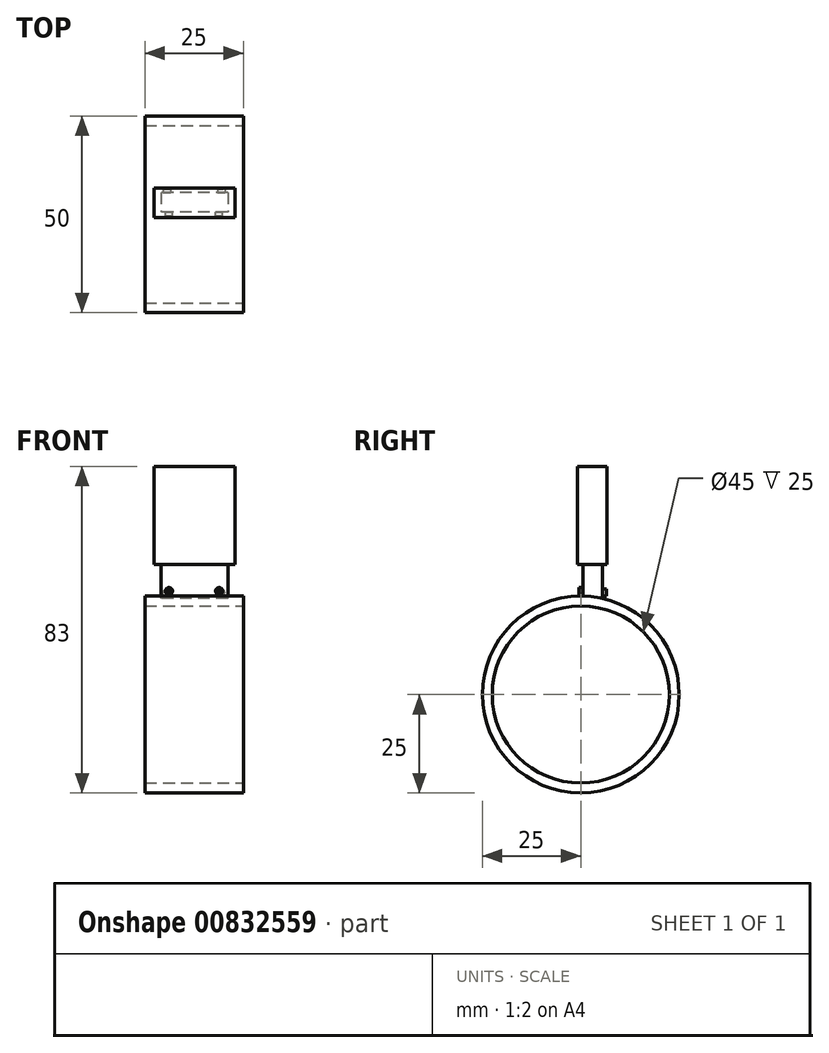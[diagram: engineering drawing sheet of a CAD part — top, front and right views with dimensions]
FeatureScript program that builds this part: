
annotation { "Feature Type Name" : "Feature", "Feature Type Description" : "" }
export const myFeature = defineFeature(function(context is Context, id is Id, definition is map)
    precondition{}
    {
        {
            var Q0;
            Q0=qCreatedBy(makeId("Right.planeOp"),FACE);
            var sketch = newSketch(context, id + "F0", { "sketchPlane" : qUnion([Q0])});
            skCircle(sketch, "E0", {"center": v(0, 0) * mm, "radius": 25 * mm});
            skSolve(sketch);
        }
        {
            var Q0;
            Q0=makeQuery(id+"F0.imprint","IMPRINT",FACE,{"disambiguationData":[TD([[makeQuery(id+"F0.imprint","IMPRINT",EDGE,{"derivedFrom":sQuery(id+"F0.wireOp",EDGE,"E0")}),1.0]])]});
            extrude(context, id + "F1", {"entities" : qUnion([Q0]), "depth" : 25 * mm, "offsetDistance" : 25 * mm});
        }
        {
            var Q0;
            Q0=makeQuery(id+"F1.opExtrude","CAP_FACE",FACE,{"disambiguationData":[OSD([sQuery(id+"F0.wireOp",EDGE,"E0")])],"isStart":false});
            var sketch = newSketch(context, id + "F2", { "sketchPlane" : qUnion([Q0])});
            skCircle(sketch, "E1", {"center": v(0, 0) * mm, "radius": 22.5 * mm});
            skSolve(sketch);
        }
        {
            var Q0;
            Q0=makeQuery(id+"F2.imprint","IMPRINT",FACE,{"disambiguationData":[TD([[makeQuery(id+"F2.imprint","IMPRINT",EDGE,{"derivedFrom":sQuery(id+"F2.wireOp",EDGE,"E1")}),1.0]])]});
            extrude(context, id + "F3", {"entities" : qUnion([Q0]), "operationType" : NewBodyOperationType.REMOVE, "oppositeDirection" : true, "depth" : 30 * mm, "offsetDistance" : 25 * mm});
        }
        {
            var Q0;
            Q0=qCreatedBy(makeId("Top.planeOp"),FACE);
            cPlane(context, id + "F4", {"entities" : qUnion([Q0]), "cplaneType" : CPlaneType.OFFSET, "offset" : 23 * mm, "width" : 150 * mm, "height" : 150 * mm});
        }
        {
            var Q0;
            Q0=qCreatedBy(id+"F4.planeOp",FACE);
            var sketch = newSketch(context, id + "F5", { "sketchPlane" : qUnion([Q0])});
            skLineSegment(sketch, "E2", {"start": v(4.05, 5.56) * mm, "end": v(4.05, 0.56) * mm});
            skLineSegment(sketch, "E3", {"start": v(4.05, 5.56) * mm, "end": v(21.05, 5.56) * mm});
            skLineSegment(sketch, "E4", {"start": v(4.05, 0.56) * mm, "end": v(21.05, 0.56) * mm});
            skLineSegment(sketch, "E5", {"start": v(21.05, 5.56) * mm, "end": v(21.05, 0.56) * mm});
            skSolve(sketch);
        }
        {
            var Q0;
            Q0 = qSketchRegion(id + "F5", true);
            extrude(context, id + "F6", {"entities" : qUnion([Q0]), "operationType" : NewBodyOperationType.ADD, "depth" : 10 * mm, "offsetDistance" : 25 * mm});
        }
        {
            var Q0;
            Q0=makeQuery(id+"F6.opExtrude","SWEPT_FACE",FACE,{"disambiguationData":[OSD([sQuery(id+"F5.wireOp",EDGE,"E3")])]});
            var sketch = newSketch(context, id + "F7", { "sketchPlane" : qUnion([Q0])});
            skCircle(sketch, "E6", {"center": v(-19.39, 25.93) * mm, "radius": 0.9 * mm});
            skCircle(sketch, "E7", {"center": v(-5.54, 25.93) * mm, "radius": 0.9 * mm});
            skSolve(sketch);
        }
        {
            var Q0;
            Q0=makeQuery(id+"F7.imprint","IMPRINT",FACE,{"disambiguationData":[TD([[makeQuery(id+"F7.imprint","IMPRINT",EDGE,{"derivedFrom":sQuery(id+"F7.wireOp",EDGE,"E6")}),1.0]])]});
            var Q1;
            Q1=makeQuery(id+"F7.imprint","IMPRINT",FACE,{"disambiguationData":[TD([[makeQuery(id+"F7.imprint","IMPRINT",EDGE,{"derivedFrom":sQuery(id+"F7.wireOp",EDGE,"E7")}),1.0]])]});
            extrude(context, id + "F8", {"entities" : qUnion([Q0, Q1]), "operationType" : NewBodyOperationType.ADD, "depth" : 1 * mm, "offsetDistance" : 25 * mm});
        }
        {
            var Q0;
            Q0=makeQuery(id+"F8.opExtrude","CAP_FACE",FACE,{"disambiguationData":[OSD([sQuery(id+"F7.wireOp",EDGE,"E6")])],"isStart":false});
            var sketch = newSketch(context, id + "F9", { "sketchPlane" : qUnion([Q0])});
            skLineSegment(sketch, "E8.bottom", {"start": v(-19.88, 25.88) * mm, "end": v(-18.78, 25.88) * mm});
            skLineSegment(sketch, "E8.top", {"start": v(-19.88, 26) * mm, "end": v(-18.78, 26) * mm});
            skLineSegment(sketch, "E8.left", {"start": v(-19.88, 25.88) * mm, "end": v(-19.88, 26) * mm});
            skLineSegment(sketch, "E8.right", {"start": v(-18.78, 25.88) * mm, "end": v(-18.78, 26) * mm});
            skLineSegment(sketch, "E9.bottom", {"start": v(-19.42, 25.36) * mm, "end": v(-19.27, 25.36) * mm});
            skLineSegment(sketch, "E9.top", {"start": v(-19.42, 26.45) * mm, "end": v(-19.27, 26.45) * mm});
            skLineSegment(sketch, "E9.left", {"start": v(-19.42, 25.36) * mm, "end": v(-19.42, 26.45) * mm});
            skLineSegment(sketch, "E9.right", {"start": v(-19.27, 25.36) * mm, "end": v(-19.27, 26.45) * mm});
            skSolve(sketch);
        }
        {
            var Q0;
            Q0 = qSketchRegion(id + "F9", true);
            extrude(context, id + "F10", {"entities" : qUnion([Q0]), "operationType" : NewBodyOperationType.REMOVE, "oppositeDirection" : true, "depth" : 0.2 * mm, "offsetDistance" : 25 * mm});
        }
        {
            var Q0;
            Q0=makeQuery(id+"F8.opExtrude","CAP_FACE",FACE,{"disambiguationData":[OSD([sQuery(id+"F7.wireOp",EDGE,"E7")])],"isStart":false});
            var sketch = newSketch(context, id + "F11", { "sketchPlane" : qUnion([Q0])});
            skLineSegment(sketch, "E10.bottom", {"start": v(-5.67, 25.28) * mm, "end": v(-5.5, 25.28) * mm});
            skLineSegment(sketch, "E10.top", {"start": v(-5.67, 26.6) * mm, "end": v(-5.5, 26.6) * mm});
            skLineSegment(sketch, "E10.left", {"start": v(-5.67, 25.28) * mm, "end": v(-5.67, 26.6) * mm});
            skLineSegment(sketch, "E10.right", {"start": v(-5.5, 25.28) * mm, "end": v(-5.5, 26.6) * mm});
            skLineSegment(sketch, "E11.bottom", {"start": v(-6.2, 25.81) * mm, "end": v(-4.92, 25.81) * mm});
            skLineSegment(sketch, "E11.top", {"start": v(-6.2, 26) * mm, "end": v(-4.92, 26) * mm});
            skLineSegment(sketch, "E11.left", {"start": v(-6.2, 25.81) * mm, "end": v(-6.2, 26) * mm});
            skLineSegment(sketch, "E11.right", {"start": v(-4.92, 25.81) * mm, "end": v(-4.92, 26) * mm});
            skSolve(sketch);
        }
        {
            var Q0;
            Q0 = qSketchRegion(id + "F11", true);
            extrude(context, id + "F12", {"entities" : qUnion([Q0]), "operationType" : NewBodyOperationType.REMOVE, "oppositeDirection" : true, "depth" : 0.2 * mm, "offsetDistance" : 25 * mm});
        }
        {
            var Q0;
            Q0=makeQuery(id+"F6.opExtrude","SWEPT_FACE",FACE,{"disambiguationData":[OSD([sQuery(id+"F5.wireOp",EDGE,"E4")])]});
            var sketch = newSketch(context, id + "F13", { "sketchPlane" : qUnion([Q0])});
            skCircle(sketch, "E12", {"center": v(6.1, 26.28) * mm, "radius": 0.9 * mm});
            skCircle(sketch, "E13", {"center": v(18.83, 26.28) * mm, "radius": 0.9 * mm});
            skSolve(sketch);
        }
        {
            var Q0;
            Q0=makeQuery(id+"F13.imprint","IMPRINT",FACE,{"disambiguationData":[TD([[makeQuery(id+"F13.imprint","IMPRINT",EDGE,{"derivedFrom":sQuery(id+"F13.wireOp",EDGE,"E12")}),1.0]])]});
            var Q1;
            Q1=makeQuery(id+"F13.imprint","IMPRINT",FACE,{"disambiguationData":[TD([[makeQuery(id+"F13.imprint","IMPRINT",EDGE,{"derivedFrom":sQuery(id+"F13.wireOp",EDGE,"E13")}),1.0]])]});
            extrude(context, id + "F14", {"entities" : qUnion([Q0, Q1]), "operationType" : NewBodyOperationType.ADD, "depth" : 1 * mm, "offsetDistance" : 25 * mm});
        }
        {
            var Q0;
            Q0=makeQuery(id+"F14.opExtrude","CAP_FACE",FACE,{"disambiguationData":[OSD([sQuery(id+"F13.wireOp",EDGE,"E12")])],"isStart":false});
            var sketch = newSketch(context, id + "F15", { "sketchPlane" : qUnion([Q0])});
            skLineSegment(sketch, "E14.bottom", {"start": v(6, 26.9) * mm, "end": v(6.13, 26.9) * mm});
            skLineSegment(sketch, "E14.top", {"start": v(6, 25.73) * mm, "end": v(6.13, 25.73) * mm});
            skLineSegment(sketch, "E14.left", {"start": v(5.96, 26.37) * mm, "end": v(5.96, 26.27) * mm});
            skLineSegment(sketch, "E14.right", {"start": v(6.2, 26.37) * mm, "end": v(6.2, 26.27) * mm});
            skLineSegment(sketch, "E15.right", {"start": v(6.73, 26.44) * mm, "end": v(6.73, 26.18) * mm});
            skLineSegment(sketch, "E16", {"start": v(5.49, 26.37) * mm, "end": v(6.73, 26.37) * mm});
            skPoint(sketch, "E16.endSnap0", {"position": v(6.73, 26.3) * mm});
            skLineSegment(sketch, "E17", {"start": v(5.49, 26.27) * mm, "end": v(6.73, 26.27) * mm});
            skLineSegment(sketch, "E18", {"start": v(6, 26.9) * mm, "end": v(6, 25.73) * mm});
            skLineSegment(sketch, "E19", {"start": v(6.13, 26.9) * mm, "end": v(6.13, 25.73) * mm});
            skLineSegment(sketch, "E20.trimOffspring", {"start": v(6, 26.44) * mm, "end": v(6.13, 26.44) * mm});
            skPoint(sketch, "E21.orphan", {"position": v(5.96, 25.73) * mm});
            skLineSegment(sketch, "E22", {"start": v(5.49, 26.37) * mm, "end": v(5.49, 26.27) * mm});
            skSolve(sketch);
        }
        {
            var Q0;
            Q0=makeQuery(id+"F14.opExtrude","CAP_FACE",FACE,{"disambiguationData":[OSD([sQuery(id+"F13.wireOp",EDGE,"E13")])],"isStart":false});
            var sketch = newSketch(context, id + "F16", { "sketchPlane" : qUnion([Q0])});
            skLineSegment(sketch, "E23.bottom", {"start": v(18.7, 26.95) * mm, "end": v(18.86, 26.95) * mm});
            skLineSegment(sketch, "E23.top", {"start": v(18.7, 25.55) * mm, "end": v(18.86, 25.55) * mm});
            skLineSegment(sketch, "E24.left", {"start": v(18.18, 26.34) * mm, "end": v(18.18, 26.21) * mm});
            skLineSegment(sketch, "E24.right", {"start": v(19.46, 26.34) * mm, "end": v(19.46, 26.21) * mm});
            skLineSegment(sketch, "E25", {"start": v(18.7, 26.95) * mm, "end": v(18.7, 25.55) * mm});
            skLineSegment(sketch, "E26", {"start": v(18.86, 26.95) * mm, "end": v(18.86, 25.55) * mm});
            skLineSegment(sketch, "E27", {"start": v(18.18, 26.34) * mm, "end": v(19.46, 26.34) * mm});
            skLineSegment(sketch, "E28", {"start": v(18.18, 26.21) * mm, "end": v(19.46, 26.21) * mm});
            skPoint(sketch, "E29.orphan", {"position": v(19.46, 26.12) * mm});
            skPoint(sketch, "E30.orphan", {"position": v(18.63, 25.55) * mm});
            skSolve(sketch);
        }
        {
            var Q0;
            Q0 = qSketchRegion(id + "F16", true);
            extrude(context, id + "F17", {"entities" : qUnion([Q0]), "operationType" : NewBodyOperationType.REMOVE, "oppositeDirection" : true, "depth" : 0.2 * mm, "offsetDistance" : 25 * mm});
        }
        {
            var Q0;
            Q0 = qSketchRegion(id + "F15", true);
            extrude(context, id + "F18", {"entities" : qUnion([Q0]), "operationType" : NewBodyOperationType.REMOVE, "oppositeDirection" : true, "depth" : 0.2 * mm, "offsetDistance" : 25 * mm});
        }
        {
            var Q0;
            Q0=makeQuery(id+"F6.opExtrude","CAP_FACE",FACE,{"disambiguationData":[OSD([sQuery(id+"F5.wireOp",EDGE,"E2"),sQuery(id+"F5.wireOp",EDGE,"E3"),sQuery(id+"F5.wireOp",EDGE,"E4"),sQuery(id+"F5.wireOp",EDGE,"E5")])],"isStart":false});
            var sketch = newSketch(context, id + "F19", { "sketchPlane" : qUnion([Q0])});
            skLineSegment(sketch, "E31.bottom", {"start": v(2.3, 6.7) * mm, "end": v(22.9, 6.7) * mm});
            skLineSegment(sketch, "E31.top", {"start": v(2.3, -0.87) * mm, "end": v(22.9, -0.87) * mm});
            skLineSegment(sketch, "E31.left", {"start": v(2.3, 6.7) * mm, "end": v(2.3, -0.87) * mm});
            skLineSegment(sketch, "E31.right", {"start": v(22.9, 6.7) * mm, "end": v(22.9, -0.87) * mm});
            skSolve(sketch);
        }
        {
            var Q0;
            Q0=makeQuery(id+"F19.imprint","IMPRINT",FACE,{"disambiguationData":[TD([[makeQuery(id+"F19.imprint","IMPRINT",EDGE,{"derivedFrom":sQuery(id+"F19.wireOp",EDGE,"E31.bottom")}),-1.0]])]});
            var Q1;
            Q1=makeQuery(id+"F19.imprint","IMPRINT",FACE,{"disambiguationData":[TD([[makeQuery(id+"F19.imprint","IMPRINT",EDGE,{"derivedFrom":makeQuery(id+"F6.opExtrude","CAP_EDGE",EDGE,{"disambiguationData":[OSD([sQuery(id+"F5.wireOp",EDGE,"E2")])],"isStart":false})}),1.0]])]});
            extrude(context, id + "F20", {"entities" : qUnion([Q0, Q1]), "operationType" : NewBodyOperationType.ADD, "depth" : 25 * mm, "offsetDistance" : 25 * mm});
        }
    });
